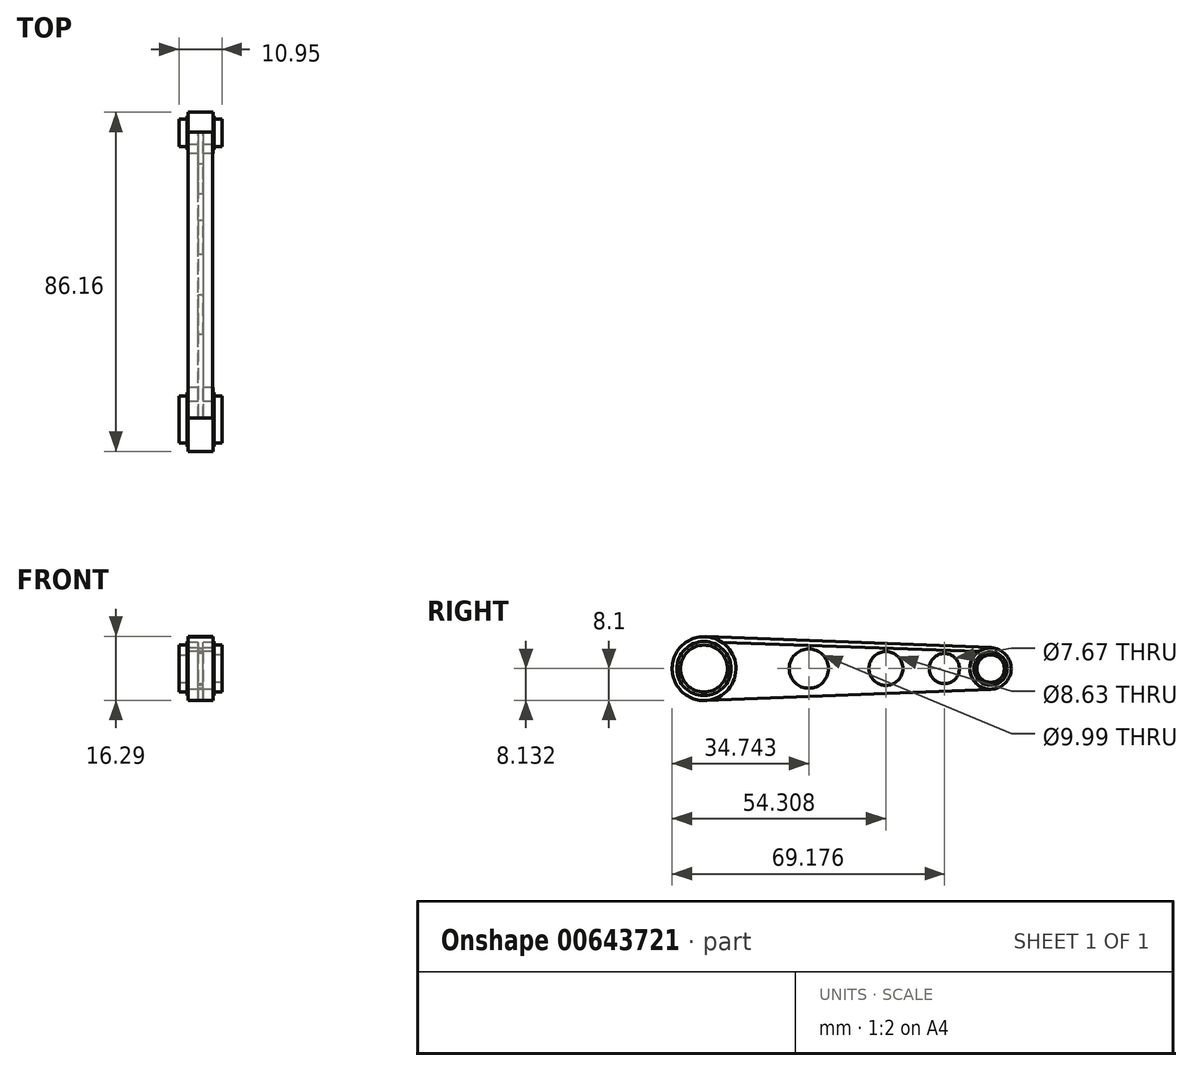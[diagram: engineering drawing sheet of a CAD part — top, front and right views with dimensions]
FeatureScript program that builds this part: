
annotation { "Feature Type Name" : "Feature", "Feature Type Description" : "" }
export const myFeature = defineFeature(function(context is Context, id is Id, definition is map)
    precondition{}
    {
        {
            var Q0;
            Q0=qCreatedBy(makeId("Right.planeOp"),FACE);
            var sketch = newSketch(context, id + "F0", { "sketchPlane" : qUnion([Q0])});
            skCircle(sketch, "E0", {"center": v(-42.23, 0) * mm, "radius": 5.96 * mm});
            skCircle(sketch, "E1", {"center": v(30.58, 0) * mm, "radius": 3.5 * mm});
            skCircle(sketch, "E2", {"center": v(-15.59, 0) * mm, "radius": 5 * mm});
            skCircle(sketch, "E3", {"center": v(3.98, 0.03) * mm, "radius": 4.31 * mm});
            skCircle(sketch, "E4", {"center": v(18.85, 0) * mm, "radius": 3.83 * mm});
            skCircle(sketch, "E5", {"center": v(-42.23, 0) * mm, "radius": 6.88 * mm});
            skCircle(sketch, "E6", {"center": v(30.58, 0) * mm, "radius": 4.23 * mm});
            skCircle(sketch, "E7", {"center": v(30.58, 0) * mm, "radius": 5.25 * mm});
            skCircle(sketch, "E8", {"center": v(-42.23, 0) * mm, "radius": 8.1 * mm});
            skLineSegment(sketch, "E9", {"start": v(-41.58, 8.08) * mm, "end": v(30.78, 5.25) * mm});
            skLineSegment(sketch, "E10", {"start": v(30.68, -5.25) * mm, "end": v(-41.9, -8.1) * mm});
            skSolve(sketch);
        }
        {
            var Q0;
            Q0=makeQuery(id+"F0.imprint","IMPRINT",FACE,{"disambiguationData":[TD([[makeQuery(id+"F0.imprint","IMPRINT",EDGE,{"derivedFrom":sQuery(id+"F0.wireOp",EDGE,"E2")}),-1.0]])]});
            extrude(context, id + "F1", {"entities" : qUnion([Q0]), "depth" : 1.27 * mm, "offsetDistance" : 25.4 * mm});
        }
        {
            var Q0;
            Q0=makeQuery(id+"F0.imprint","IMPRINT",FACE,{"disambiguationData":[TD([[makeQuery(id+"F0.imprint","IMPRINT",EDGE,{"derivedFrom":sQuery(id+"F0.wireOp",EDGE,"E5")}),-1.0]])]});
            var Q1;
            Q1=makeQuery(id+"F0.imprint","IMPRINT",FACE,{"disambiguationData":[TD([[makeQuery(id+"F0.imprint","IMPRINT",EDGE,{"derivedFrom":sQuery(id+"F0.wireOp",EDGE,"E6")}),-1.0]])]});
            extrude(context, id + "F2", {"entities" : qUnion([Q0, Q1]), "operationType" : NewBodyOperationType.ADD, "depth" : 3.8 * mm, "offsetDistance" : 25.4 * mm});
        }
        {
            var Q0;
            Q0=makeQuery(id+"F0.imprint","IMPRINT",FACE,{"disambiguationData":[TD([[makeQuery(id+"F0.imprint","IMPRINT",EDGE,{"derivedFrom":sQuery(id+"F0.wireOp",EDGE,"E5")}),-1.0]])]});
            var Q1;
            Q1=makeQuery(id+"F0.imprint","IMPRINT",FACE,{"disambiguationData":[TD([[makeQuery(id+"F0.imprint","IMPRINT",EDGE,{"derivedFrom":sQuery(id+"F0.wireOp",EDGE,"E6")}),-1.0]])]});
            extrude(context, id + "F3", {"entities" : qUnion([Q0, Q1]), "operationType" : NewBodyOperationType.ADD, "oppositeDirection" : true, "depth" : 2.54 * mm, "offsetDistance" : 25.4 * mm});
        }
        {
            var Q0;
            Q0=qCreatedBy(makeId("Right.planeOp"),FACE);
            var sketch = newSketch(context, id + "F4", { "sketchPlane" : qUnion([Q0])});
            skLineSegment(sketch, "E11", {"start": v(30.79, 5.4) * mm, "end": v(-41.79, 8.19) * mm});
            skLineSegment(sketch, "E12", {"start": v(-41.79, 8.19) * mm, "end": v(-41.79, 6.8) * mm});
            skLineSegment(sketch, "E13", {"start": v(-41.79, 6.8) * mm, "end": v(30.7, 4.2) * mm});
            skLineSegment(sketch, "E14", {"start": v(30.7, 4.2) * mm, "end": v(30.79, 5.4) * mm});
            skSolve(sketch);
        }
        {
            var Q0;
            Q0=qSketchRegion(id+"F4",true);
            extrude(context, id + "F5", {"entities" : qUnion([Q0]), "operationType" : NewBodyOperationType.ADD, "oppositeDirection" : true, "depth" : 2.54 * mm, "offsetDistance" : 25.4 * mm});
        }
        {
            var Q0;
            Q0=qSketchRegion(id+"F4",true);
            var Q1;
            Q1=makeQuery(id+"F4.imprint","IMPRINT",FACE,{"disambiguationData":[TD([[makeQuery(id+"F4.imprint","IMPRINT",EDGE,{"derivedFrom":sQuery(id+"F4.wireOp",EDGE,"E11")}),1.0]])]});
            extrude(context, id + "F6", {"entities" : qUnion([Q0, Q1]), "operationType" : NewBodyOperationType.ADD, "oppositeDirection" : true, "depth" : 2.5 * mm, "offsetDistance" : 25.4 * mm});
        }
        {
            var Q0;
            Q0=makeQuery(id+"F0.imprint","IMPRINT",FACE,{"disambiguationData":[TD([[makeQuery(id+"F0.imprint","IMPRINT",EDGE,{"derivedFrom":sQuery(id+"F0.wireOp",EDGE,"E0")}),-1.0]])]});
            var Q1;
            Q1=makeQuery(id+"F0.imprint","IMPRINT",FACE,{"disambiguationData":[TD([[makeQuery(id+"F0.imprint","IMPRINT",EDGE,{"derivedFrom":sQuery(id+"F0.wireOp",EDGE,"E1")}),-1.0]])]});
            extrude(context, id + "F7", {"entities" : qUnion([Q0, Q1]), "operationType" : NewBodyOperationType.ADD, "depth" : 1.78 * mm, "offsetDistance" : 25.4 * mm});
        }
        {
            var Q0;
            Q0=makeQuery(id+"F4.imprint","IMPRINT",FACE,{"disambiguationData":[TD([[makeQuery(id+"F4.imprint","IMPRINT",EDGE,{"derivedFrom":sQuery(id+"F4.wireOp",EDGE,"E11")}),1.0]])]});
            extrude(context, id + "F8", {"entities" : qUnion([Q0]), "operationType" : NewBodyOperationType.ADD, "depth" : 3.66 * mm, "offsetDistance" : 25.4 * mm});
        }
        {
            var Q0;
            Q0=makeQuery(id+"F0.imprint","IMPRINT",FACE,{"disambiguationData":[TD([[makeQuery(id+"F0.imprint","IMPRINT",EDGE,{"derivedFrom":sQuery(id+"F0.wireOp",EDGE,"E1")}),-1.0]])]});
            var Q1;
            Q1=makeQuery(id+"F0.imprint","IMPRINT",FACE,{"disambiguationData":[TD([[makeQuery(id+"F0.imprint","IMPRINT",EDGE,{"derivedFrom":sQuery(id+"F0.wireOp",EDGE,"E0")}),-1.0]])]});
            extrude(context, id + "F9", {"entities" : qUnion([Q0, Q1]), "operationType" : NewBodyOperationType.ADD, "depth" : 4.06 * mm, "offsetDistance" : 25.4 * mm});
        }
        {
            var Q0;
            Q0=makeQuery(id+"F0.imprint","IMPRINT",FACE,{"disambiguationData":[TD([[makeQuery(id+"F0.imprint","IMPRINT",EDGE,{"derivedFrom":sQuery(id+"F0.wireOp",EDGE,"E0")}),-1.0]])]});
            extrude(context, id + "F10", {"entities" : qUnion([Q0]), "operationType" : NewBodyOperationType.ADD, "oppositeDirection" : true, "depth" : 2.8 * mm, "offsetDistance" : 25.4 * mm});
        }
        {
            var Q0;
            Q0=makeQuery(id+"F0.imprint","IMPRINT",FACE,{"disambiguationData":[TD([[makeQuery(id+"F0.imprint","IMPRINT",EDGE,{"derivedFrom":sQuery(id+"F0.wireOp",EDGE,"E1")}),-1.0]])]});
            extrude(context, id + "F11", {"entities" : qUnion([Q0]), "operationType" : NewBodyOperationType.ADD, "oppositeDirection" : true, "depth" : 2.77 * mm, "offsetDistance" : 25.4 * mm});
        }
        {
            var Q0;
            Q0=makeQuery(id+"F0.imprint","IMPRINT",FACE,{"disambiguationData":[TD([[makeQuery(id+"F0.imprint","IMPRINT",EDGE,{"derivedFrom":sQuery(id+"F0.wireOp",EDGE,"E0")}),1.0]])]});
            var Q1;
            Q1=makeQuery(id+"F0.imprint","IMPRINT",FACE,{"disambiguationData":[TD([[makeQuery(id+"F0.imprint","IMPRINT",EDGE,{"derivedFrom":sQuery(id+"F0.wireOp",EDGE,"E1")}),1.0]])]});
            extrude(context, id + "F12", {"entities" : qUnion([Q0, Q1]), "operationType" : NewBodyOperationType.ADD, "depth" : 6.1 * mm, "offsetDistance" : 25.4 * mm});
        }
        {
            var Q0;
            Q0=makeQuery(id+"F0.imprint","IMPRINT",FACE,{"disambiguationData":[TD([[makeQuery(id+"F0.imprint","IMPRINT",EDGE,{"derivedFrom":sQuery(id+"F0.wireOp",EDGE,"E1")}),1.0]])]});
            var Q1;
            Q1=makeQuery(id+"F0.imprint","IMPRINT",FACE,{"disambiguationData":[TD([[makeQuery(id+"F0.imprint","IMPRINT",EDGE,{"derivedFrom":sQuery(id+"F0.wireOp",EDGE,"E0")}),1.0]])]});
            extrude(context, id + "F13", {"entities" : qUnion([Q0, Q1]), "operationType" : NewBodyOperationType.ADD, "oppositeDirection" : true, "depth" : 4.85 * mm, "offsetDistance" : 25.4 * mm});
        }
    });
